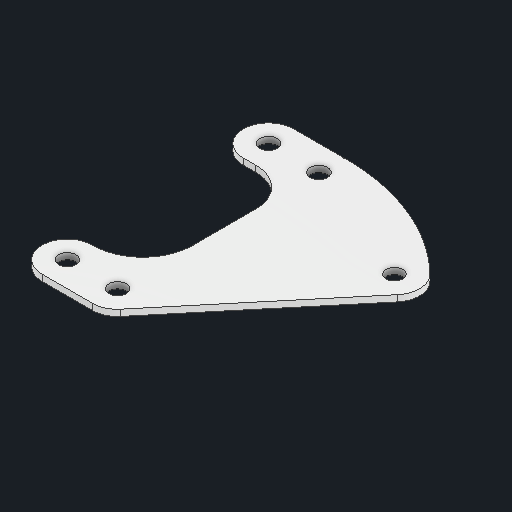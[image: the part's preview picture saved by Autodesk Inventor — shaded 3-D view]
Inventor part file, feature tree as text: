
AUTODESK INVENTOR PART (.ipt)
format: ipt  version: 2025 (Build 290162000, 162)  size: 173,056 bytes
history: native  units: in
note: dims shown in document units (in); Inventor stores cm internally (conversion verified against a paired STEP export)
features: other x4, extrude x1, sketch x1
ambient origin geometry x8: Origin, YZ Plane, XZ Plane, XY Plane, X Axis, Y Axis, Z Axis, Center Point
bodies: Solid1 (feature_tree)
feature tree (6):
  other  "Blocks"
  extrude  "Extrusion1"  Depth=0.5in
  sketch  "Sketch1"  dims[d0=0.5in d1=0.5in d2=0.375in d3=0.0625in d4=0.0in]
  other  "main"
  other  "main:1"
  other  "Definition1"
